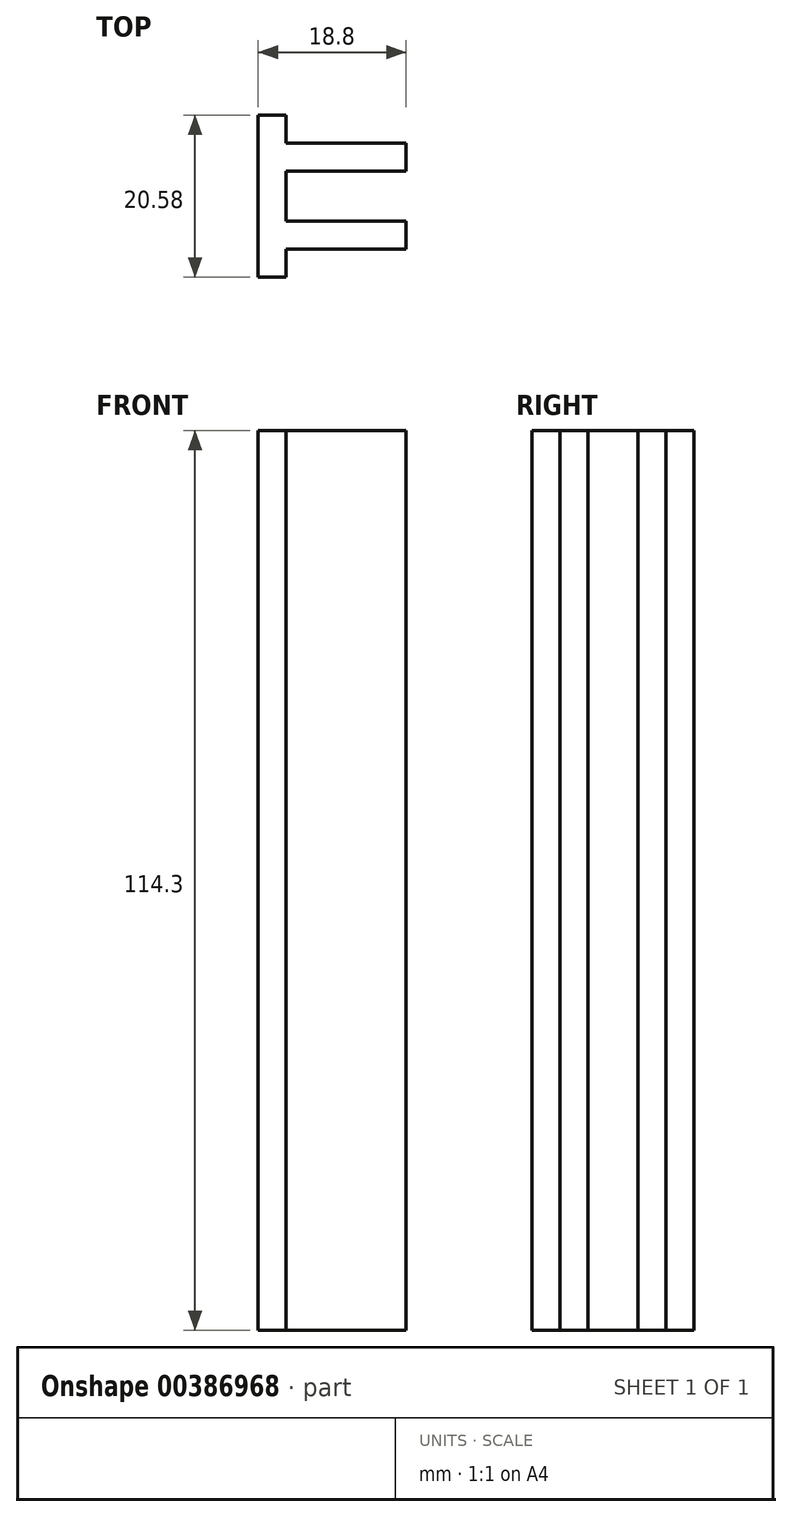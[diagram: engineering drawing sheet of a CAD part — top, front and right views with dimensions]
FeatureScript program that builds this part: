
annotation { "Feature Type Name" : "Feature", "Feature Type Description" : "" }
export const myFeature = defineFeature(function(context is Context, id is Id, definition is map)
    precondition{}
    {
        {
            var Q0;
            Q0=qCreatedBy(makeId("Top.planeOp"),FACE);
            var sketch = newSketch(context, id + "F0", { "sketchPlane" : qUnion([Q0])});
            skLineSegment(sketch, "E0.bottom", {"start": v(-7.62, 3.18) * mm, "end": v(7.62, 3.18) * mm});
            skLineSegment(sketch, "E0.top", {"start": v(-7.62, -3.18) * mm, "end": v(7.62, -3.18) * mm});
            skLineSegment(sketch, "E0.left", {"start": v(-7.62, 3.18) * mm, "end": v(-7.62, -3.18) * mm});
            skPoint(sketch, "E0.middle", {"position": v(0, 0) * mm});
            skLineSegment(sketch, "E1.top", {"start": v(-7.62, 6.73) * mm, "end": v(7.62, 6.73) * mm});
            skLineSegment(sketch, "E1.left", {"start": v(-7.62, 3.18) * mm, "end": v(-7.62, 6.73) * mm});
            skLineSegment(sketch, "E1.right", {"start": v(7.62, 3.18) * mm, "end": v(7.62, 6.73) * mm});
            skLineSegment(sketch, "E2.bottom", {"start": v(7.62, -3.17) * mm, "end": v(-7.62, -3.18) * mm});
            skLineSegment(sketch, "E2.top", {"start": v(7.62, -6.73) * mm, "end": v(-7.62, -6.73) * mm});
            skLineSegment(sketch, "E2.left", {"start": v(7.62, -3.17) * mm, "end": v(7.62, -6.73) * mm});
            skLineSegment(sketch, "E2.right", {"start": v(-7.62, -3.18) * mm, "end": v(-7.62, -6.73) * mm});
            skLineSegment(sketch, "E3.bottom", {"start": v(-7.62, -6.73) * mm, "end": v(-11.18, -6.73) * mm});
            skLineSegment(sketch, "E3.top", {"start": v(-7.62, 6.73) * mm, "end": v(-11.18, 6.73) * mm});
            skLineSegment(sketch, "E3.left", {"start": v(-7.62, -6.73) * mm, "end": v(-7.62, 6.73) * mm});
            skLineSegment(sketch, "E3.right", {"start": v(-11.18, -6.73) * mm, "end": v(-11.18, 6.73) * mm});
            skLineSegment(sketch, "E4.bottom", {"start": v(-11.18, 6.73) * mm, "end": v(-7.62, 6.73) * mm});
            skLineSegment(sketch, "E4.top", {"start": v(-11.18, 10.29) * mm, "end": v(-7.62, 10.29) * mm});
            skLineSegment(sketch, "E4.left", {"start": v(-11.18, 6.73) * mm, "end": v(-11.18, 10.29) * mm});
            skLineSegment(sketch, "E4.right", {"start": v(-7.62, 6.73) * mm, "end": v(-7.62, 10.29) * mm});
            skLineSegment(sketch, "E5.bottom", {"start": v(-11.18, -6.73) * mm, "end": v(-7.62, -6.73) * mm});
            skLineSegment(sketch, "E5.top", {"start": v(-11.18, -10.29) * mm, "end": v(-7.62, -10.29) * mm});
            skLineSegment(sketch, "E5.left", {"start": v(-11.18, -6.73) * mm, "end": v(-11.18, -10.29) * mm});
            skLineSegment(sketch, "E5.right", {"start": v(-7.62, -6.73) * mm, "end": v(-7.62, -10.29) * mm});
            skSolve(sketch);
        }
        {
            var Q0;
            Q0=makeQuery(id+"F0.imprint","IMPRINT",FACE,{"disambiguationData":[TD([[makeQuery(id+"F0.imprint","IMPRINT",EDGE,{"derivedFrom":sQuery(id+"F0.wireOp",EDGE,"E0.left")}),-1.0]])]});
            var Q1;
            Q1=makeQuery(id+"F0.imprint","IMPRINT",FACE,{"disambiguationData":[TD([[makeQuery(id+"F0.imprint","IMPRINT",EDGE,{"derivedFrom":sQuery(id+"F0.wireOp",EDGE,"E3.top")}),-1.0]])]});
            var Q2;
            Q2=makeQuery(id+"F0.imprint","IMPRINT",FACE,{"disambiguationData":[TD([[makeQuery(id+"F0.imprint","IMPRINT",EDGE,{"derivedFrom":sQuery(id+"F0.wireOp",EDGE,"E3.bottom")}),1.0]])]});
            var Q3;
            Q3=makeQuery(id+"F0.imprint","IMPRINT",FACE,{"disambiguationData":[TD([[makeQuery(id+"F0.imprint","IMPRINT",EDGE,{"derivedFrom":sQuery(id+"F0.wireOp",EDGE,"E0.top")}),-1.0]])]});
            var Q4;
            Q4=makeQuery(id+"F0.imprint","IMPRINT",FACE,{"disambiguationData":[TD([[makeQuery(id+"F0.imprint","IMPRINT",EDGE,{"derivedFrom":sQuery(id+"F0.wireOp",EDGE,"E0.bottom")}),1.0]])]});
            extrude(context, id + "F1", {"entities" : qUnion([Q0, Q1, Q2, Q3, Q4]), "depth" : 114.3 * mm, "offsetDistance" : 25.4 * mm});
        }
    });
